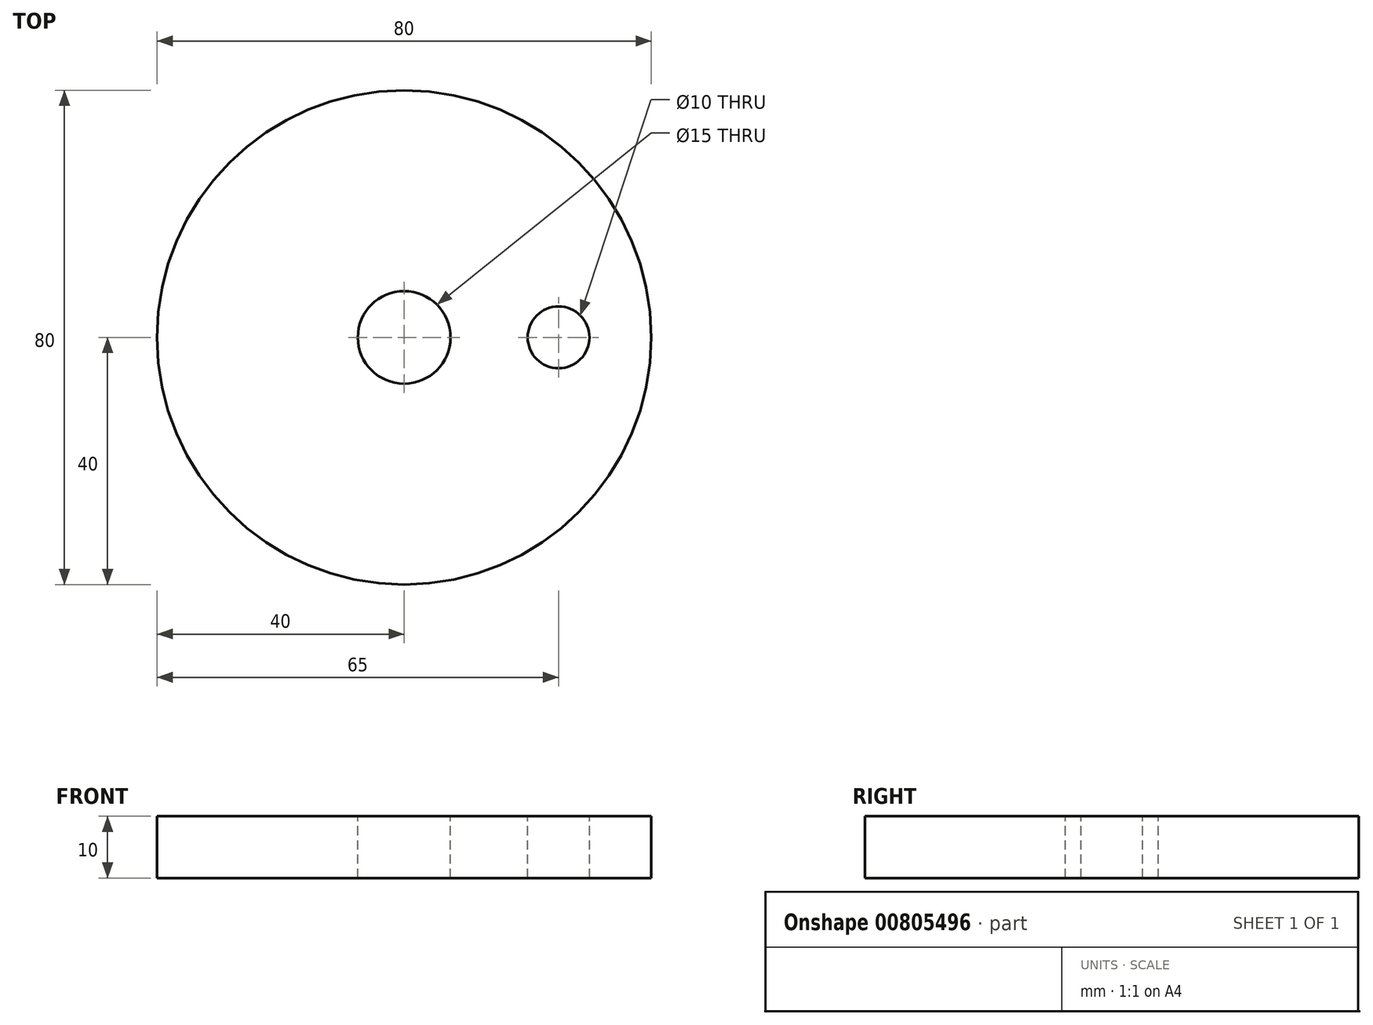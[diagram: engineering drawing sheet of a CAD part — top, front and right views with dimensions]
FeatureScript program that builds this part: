
annotation { "Feature Type Name" : "Feature", "Feature Type Description" : "" }
export const myFeature = defineFeature(function(context is Context, id is Id, definition is map)
    precondition{}
    {
        {
            var Q0;
            Q0=qCreatedBy(makeId("Top.planeOp"),FACE);
            var sketch = newSketch(context, id + "F0", { "sketchPlane" : qUnion([Q0])});
            skCircle(sketch, "E0", {"center": v(0, 0) * mm, "radius": 40 * mm});
            skSolve(sketch);
        }
        {
            var Q0;
            Q0=makeQuery(id+"F0.imprint","IMPRINT",FACE,{"disambiguationData":[TD([[makeQuery(id+"F0.imprint","IMPRINT",EDGE,{"derivedFrom":sQuery(id+"F0.wireOp",EDGE,"E0")}),1.0]])]});
            extrude(context, id + "F1", {"entities" : qUnion([Q0]), "depth" : 10 * mm});
        }
        {
            var Q0;
            Q0=makeQuery(id+"F1.opExtrude","CAP_FACE",FACE,{"disambiguationData":[OSD([sQuery(id+"F0.wireOp",EDGE,"E0")])],"isStart":false});
            var sketch = newSketch(context, id + "F2", { "sketchPlane" : qUnion([Q0])});
            skPoint(sketch, "E1", {"position": v(25, 0) * mm});
            skSolve(sketch);
        }
        {
            var Q0;
            Q0=sQuery(id+"F2.wireOp",VERTEX,"E1");
            var Q1;
            Q1=makeQuery(id+"F1.opExtrude","SWEPT_BODY",BODY,{"disambiguationData":[OSD([sQuery(id+"F0.wireOp",EDGE,"E0")])]});
            hole(context, id + "F4", {"style" : HoleStyle.SIMPLE, "endStyle" : HoleEndStyle.THROUGH, "holeDiameter" : 10 * mm, "locations" : qUnion([Q0]), "scope" : qUnion([Q1]), "isTappedThrough" : true});
        }
        {
            var Q0;
            Q0=makeQuery(id+"F1.opExtrude","CAP_FACE",FACE,{"disambiguationData":[OSD([sQuery(id+"F0.wireOp",EDGE,"E0")])],"isStart":false});
            var sketch = newSketch(context, id + "F3", { "sketchPlane" : qUnion([Q0])});
            skPoint(sketch, "E2", {"position": v(0, 0) * mm});
            skSolve(sketch);
        }
        {
            var Q0;
            Q0=sQuery(id+"F3.wireOp",VERTEX,"E2");
            var Q1;
            Q1=makeQuery(id+"F1.opExtrude","SWEPT_BODY",BODY,{"disambiguationData":[OSD([sQuery(id+"F0.wireOp",EDGE,"E0")])]});
            hole(context, id + "F5", {"style" : HoleStyle.SIMPLE, "endStyle" : HoleEndStyle.THROUGH, "holeDiameter" : 15 * mm, "locations" : qUnion([Q0]), "scope" : qUnion([Q1]), "isTappedThrough" : true});
        }
    });
